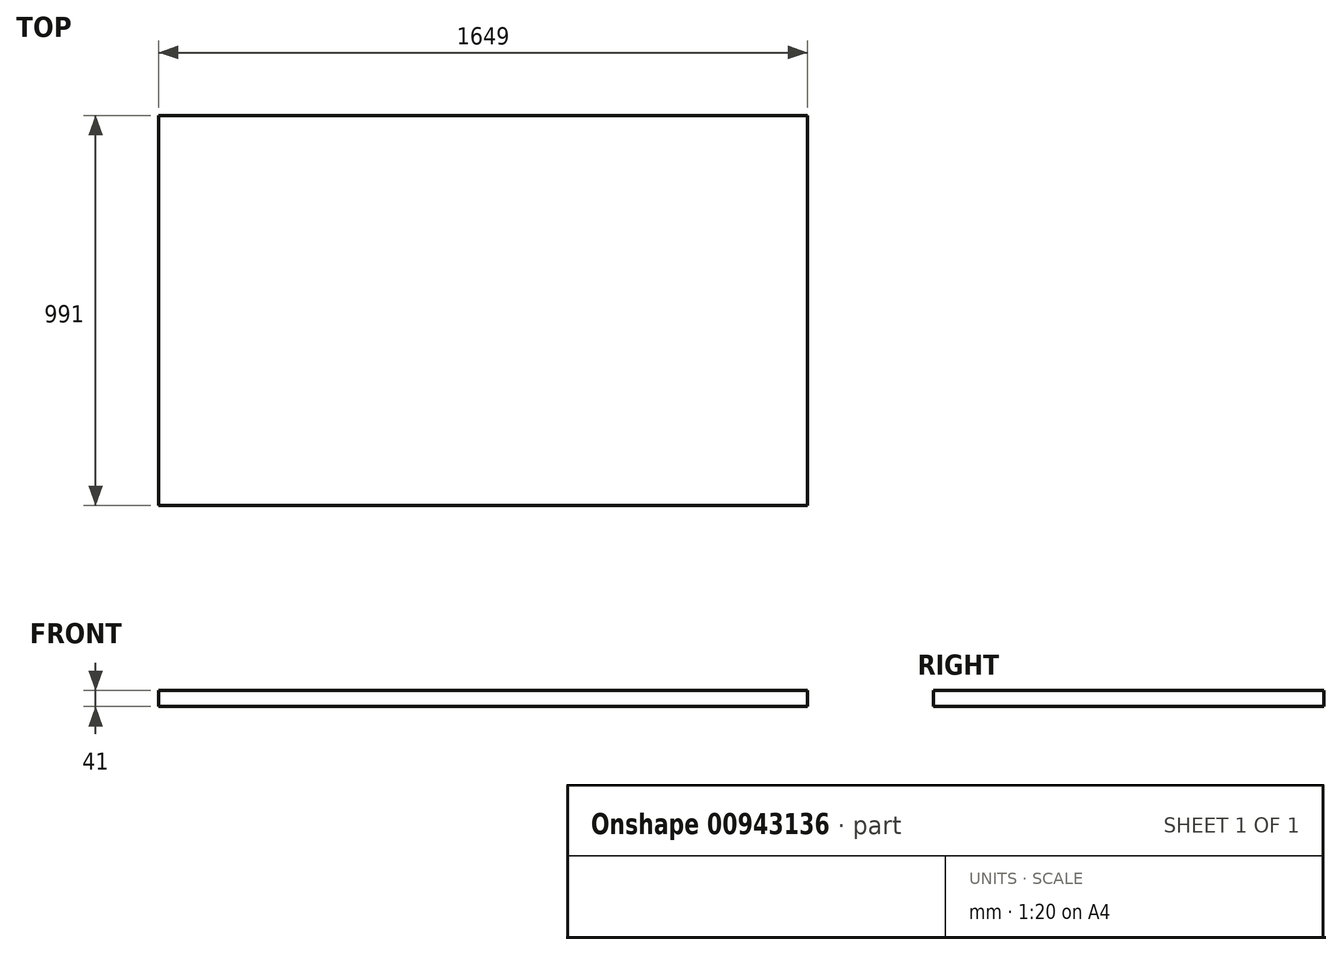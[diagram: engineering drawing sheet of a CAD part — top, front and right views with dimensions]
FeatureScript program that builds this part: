
annotation { "Feature Type Name" : "Feature", "Feature Type Description" : "" }
export const myFeature = defineFeature(function(context is Context, id is Id, definition is map)
    precondition{}
    {
        {
            var Q0;
            Q0=qCreatedBy(makeId("Top.planeOp"),FACE);
            var sketch = newSketch(context, id + "F0", { "sketchPlane" : qUnion([Q0])});
            skLineSegment(sketch, "E0.bottom", {"start": v(824.5, -495.5) * mm, "end": v(-824.5, -495.5) * mm});
            skLineSegment(sketch, "E0.top", {"start": v(824.5, 495.5) * mm, "end": v(-824.5, 495.5) * mm});
            skLineSegment(sketch, "E0.left", {"start": v(824.5, -495.5) * mm, "end": v(824.5, 495.5) * mm});
            skLineSegment(sketch, "E0.right", {"start": v(-824.5, -495.5) * mm, "end": v(-824.5, 495.5) * mm});
            skPoint(sketch, "E0.middle", {"position": v(0, 0) * mm});
            skSolve(sketch);
        }
        {
            var Q0;
            Q0=makeQuery(id+"F0.imprint","IMPRINT",FACE,{"disambiguationData":[TD([[makeQuery(id+"F0.imprint","IMPRINT",EDGE,{"derivedFrom":sQuery(id+"F0.wireOp",EDGE,"E0.bottom")}),-1.0]])]});
            extrude(context, id + "F1", {"entities" : qUnion([Q0]), "depth" : 41 * mm, "offsetDistance" : 25 * mm});
        }
    });
